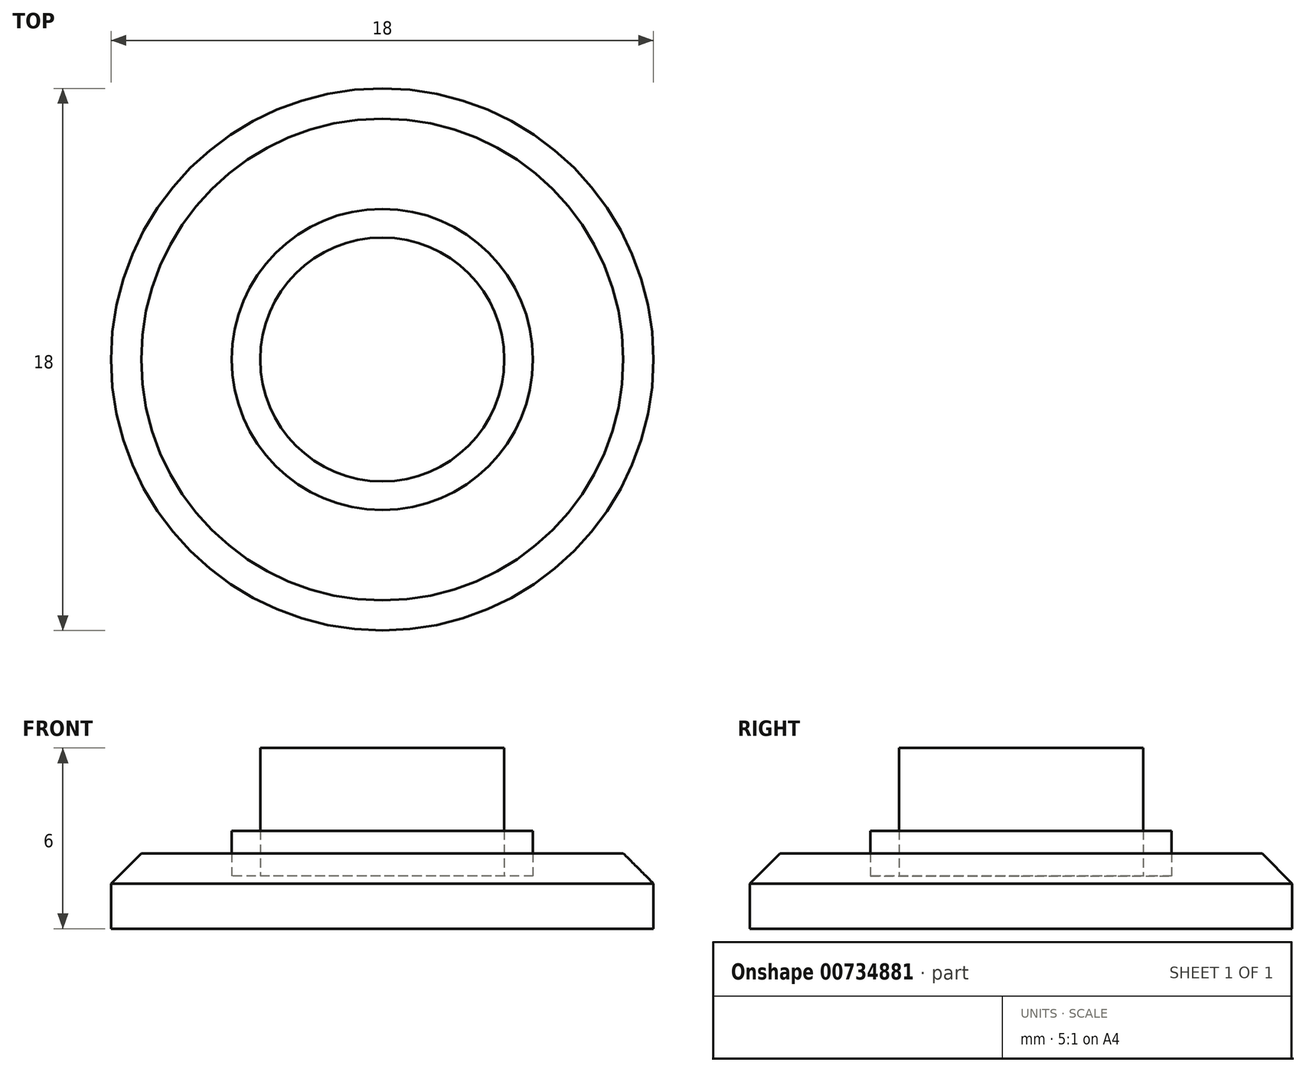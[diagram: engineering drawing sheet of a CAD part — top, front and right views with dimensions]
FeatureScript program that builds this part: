
annotation { "Feature Type Name" : "Feature", "Feature Type Description" : "" }
export const myFeature = defineFeature(function(context is Context, id is Id, definition is map)
    precondition{}
    {
        {
            var Q0;
            Q0=qCreatedBy(makeId("Top.planeOp"),FACE);
            var sketch = newSketch(context, id + "F0", { "sketchPlane" : qUnion([Q0])});
            skCircle(sketch, "E0", {"center": v(0, 0) * mm, "radius": 9 * mm});
            skCircle(sketch, "E1", {"center": v(0, 0) * mm, "radius": 4.05 * mm});
            skSolve(sketch);
        }
        {
            var Q0;
            Q0=makeQuery(id+"F0.imprint","IMPRINT",FACE,{"disambiguationData":[TD([[makeQuery(id+"F0.imprint","IMPRINT",EDGE,{"derivedFrom":sQuery(id+"F0.wireOp",EDGE,"E0")}),1.0]])]});
            extrude(context, id + "F1", {"entities" : qUnion([Q0]), "depth" : 2.5 * mm, "offsetDistance" : 25 * mm});
        }
        {
            var Q0;
            Q0=makeQuery(id+"F0.imprint","IMPRINT",FACE,{"disambiguationData":[TD([[makeQuery(id+"F0.imprint","IMPRINT",EDGE,{"derivedFrom":sQuery(id+"F0.wireOp",EDGE,"E1")}),1.0]])]});
            extrude(context, id + "F2", {"entities" : qUnion([Q0]), "operationType" : NewBodyOperationType.ADD, "depth" : 6 * mm, "offsetDistance" : 25 * mm});
        }
        {
            var Q0;
            Q0=makeQuery(id+"F1.opExtrude","CAP_FACE",FACE,{"disambiguationData":[OSD([sQuery(id+"F0.wireOp",EDGE,"E0"),sQuery(id+"F0.wireOp",EDGE,"E1")])],"isStart":false});
            var sketch = newSketch(context, id + "F3", { "sketchPlane" : qUnion([Q0])});
            skCircle(sketch, "E2", {"center": v(0, 0) * mm, "radius": 5 * mm});
            skSolve(sketch);
        }
        {
            var Q0;
            Q0=makeQuery(id+"F3.imprint","IMPRINT",FACE,{"disambiguationData":[TD([[makeQuery(id+"F3.imprint","IMPRINT",EDGE,{"derivedFrom":sQuery(id+"F3.wireOp",EDGE,"E2")}),1.0]])]});
            var Q1;
            Q1=sQuery(id+"F3.wireOp",EDGE,"E2");
            extrude(context, id + "F4", {"entities" : qUnion([Q0]), "surfaceEntities" : qUnion([Q1]), "endBound" : BoundingType.SYMMETRIC, "depth" : 1.5 * mm, "offsetDistance" : 25 * mm});
        }
        {
            var Q0;
            Q0=makeQuery(id+"F1.opExtrude","CAP_EDGE",EDGE,{"disambiguationData":[OSD([sQuery(id+"F0.wireOp",EDGE,"E0")])],"isStart":false});
            chamfer(context, id + "F5", {"entities" : qUnion([Q0]), "width" : 1 * mm, "tangentPropagation" : true});
        }
    });
